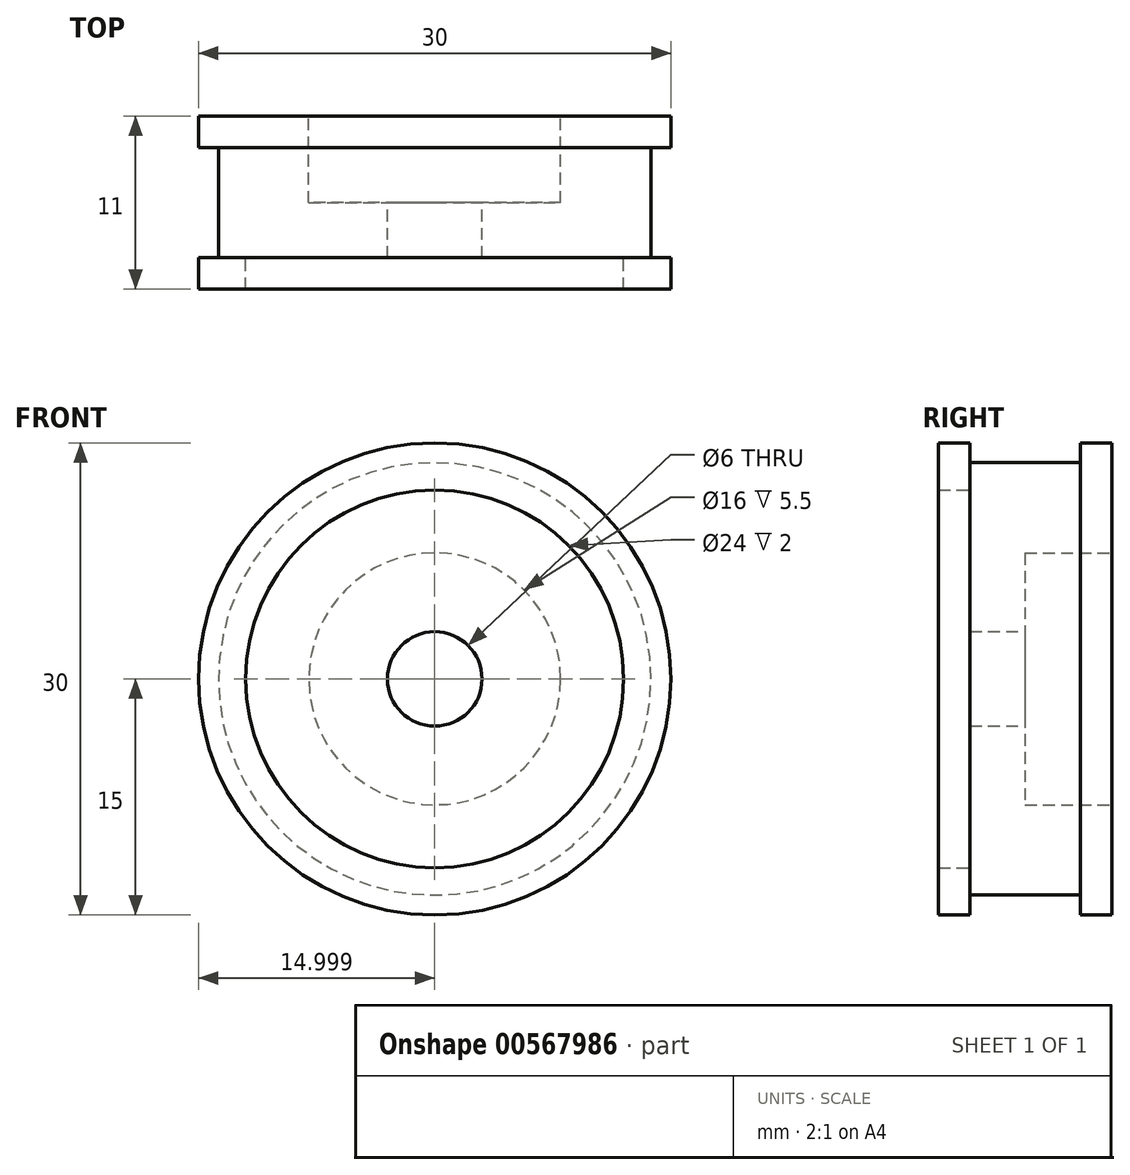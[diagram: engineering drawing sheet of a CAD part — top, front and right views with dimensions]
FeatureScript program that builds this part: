
annotation { "Feature Type Name" : "Feature", "Feature Type Description" : "" }
export const myFeature = defineFeature(function(context is Context, id is Id, definition is map)
    precondition{}
    {
        {
            var Q0;
            Q0=qCreatedBy(makeId("Top.planeOp"),FACE);
            var sketch = newSketch(context, id + "F0", { "sketchPlane" : qUnion([Q0])});
            skLineSegment(sketch, "E0", {"start": v(-36.97, 19.04) * mm, "end": v(-36.97, 17.04) * mm});
            skLineSegment(sketch, "E1", {"start": v(-36.97, 17.04) * mm, "end": v(-35.7, 17.04) * mm});
            skLineSegment(sketch, "E2", {"start": v(-35.7, 17.04) * mm, "end": v(-35.7, 10.04) * mm});
            skLineSegment(sketch, "E3", {"start": v(-35.7, 10.04) * mm, "end": v(-36.97, 10.04) * mm});
            skLineSegment(sketch, "E4", {"start": v(-36.97, 10.04) * mm, "end": v(-36.97, 8.04) * mm});
            skLineSegment(sketch, "E5", {"start": v(-24.97, 10.04) * mm, "end": v(-24.97, 13.54) * mm});
            skLineSegment(sketch, "E6", {"start": v(-24.97, 13.54) * mm, "end": v(-29.97, 13.54) * mm});
            skLineSegment(sketch, "E7", {"start": v(-29.97, 13.54) * mm, "end": v(-29.97, 19.04) * mm});
            skLineSegment(sketch, "E8", {"start": v(-29.97, 19.04) * mm, "end": v(-36.97, 19.04) * mm});
            skLineSegment(sketch, "E9", {"start": v(-36.97, 8.04) * mm, "end": v(-33.97, 8.04) * mm});
            skLineSegment(sketch, "E10", {"start": v(-33.97, 8.04) * mm, "end": v(-33.97, 10.04) * mm});
            skLineSegment(sketch, "E11", {"start": v(-33.97, 10.04) * mm, "end": v(-24.97, 10.04) * mm});
            skLineSegment(sketch, "E12", {"start": v(-21.97, 19.38) * mm, "end": v(-21.97, 7.6) * mm, "construction": true});
            skSolve(sketch);
        }
        {
            var Q0;
            Q0=makeQuery(id+"F0.imprint","IMPRINT",FACE,{"disambiguationData":[TD([[makeQuery(id+"F0.imprint","IMPRINT",EDGE,{"derivedFrom":sQuery(id+"F0.wireOp",EDGE,"E0")}),1.0]])]});
            var Q1;
            Q1=sQuery(id+"F0.wireOp",EDGE,"E12");
            revolve(context, id + "F1", {"entities" : qUnion([Q0]), "axis" : qUnion([Q1]), "revolveType" : RevolveType.FULL});
        }
    });
